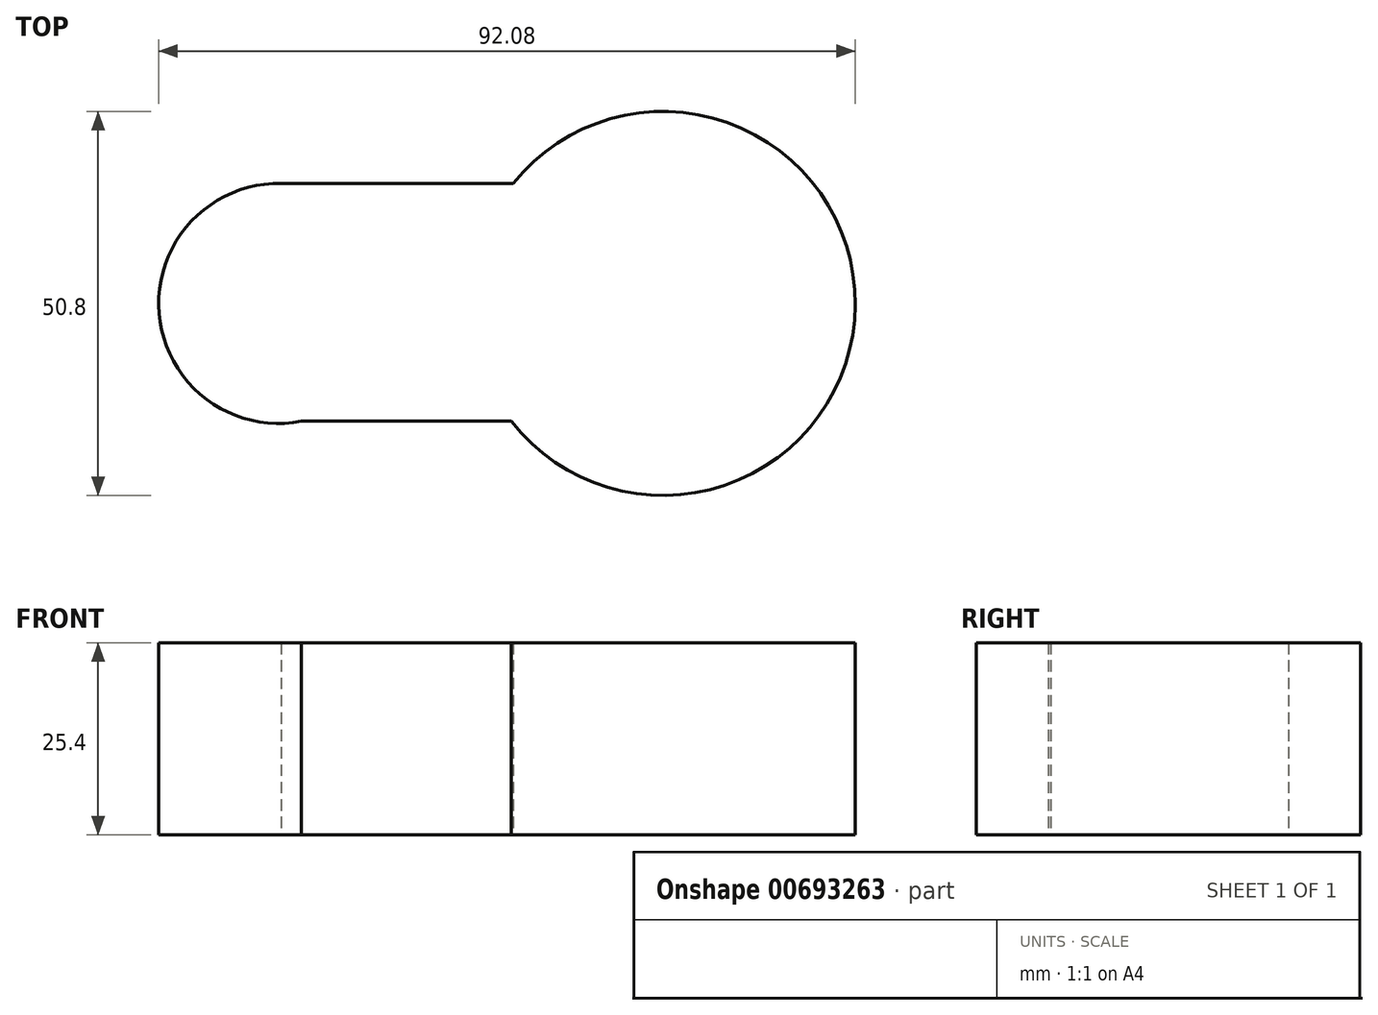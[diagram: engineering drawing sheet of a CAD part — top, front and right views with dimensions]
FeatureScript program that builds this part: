
annotation { "Feature Type Name" : "Feature", "Feature Type Description" : "" }
export const myFeature = defineFeature(function(context is Context, id is Id, definition is map)
    precondition{}
    {
        {
            var Q0;
            Q0=qCreatedBy(makeId("Top.planeOp"),FACE);
            var sketch = newSketch(context, id + "F0", { "sketchPlane" : qUnion([Q0])});
            skCircle(sketch, "E0", {"center": v(-29.75, 0) * mm, "radius": 15.88 * mm});
            skCircle(sketch, "E1", {"center": v(21.05, 0) * mm, "radius": 25.4 * mm});
            skLineSegment(sketch, "E2", {"start": v(-30.1, 15.87) * mm, "end": v(1.22, 15.87) * mm});
            skLineSegment(sketch, "E3", {"start": v(-32.76, -15.59) * mm, "end": v(1, -15.59) * mm});
            skSolve(sketch);
        }
        {
            var Q0;
            {var subQ0=sQuery(id+"F0.wireOp",EDGE,"E2");var subQ1=sQuery(id+"F0.wireOp",EDGE,"E0");var subQ2=makeQuery(id+"F0.imprint","INTERSECT",VERTEX,{"disambiguationData":[OD(0.0)],"derivedFrom":[subQ1,subQ0]});Q0=makeQuery(id+"F0.imprint","IMPRINT",FACE,{"disambiguationData":[TD([[makeQuery(id+"F0.imprint","IMPRINT",EDGE,{"disambiguationData":[TD([[subQ2,-1.0]])],"derivedFrom":subQ1}),1.0]])]});}
            var Q1;
            {var subQ0=sQuery(id+"F0.wireOp",EDGE,"E2");var subQ1=sQuery(id+"F0.wireOp",EDGE,"E0");var subQ2=makeQuery(id+"F0.imprint","INTERSECT",VERTEX,{"disambiguationData":[OD(1.0)],"derivedFrom":[subQ1,subQ0]});Q1=makeQuery(id+"F0.imprint","IMPRINT",FACE,{"disambiguationData":[TD([[makeQuery(id+"F0.imprint","IMPRINT",EDGE,{"disambiguationData":[TD([[subQ2,1.0]])],"derivedFrom":subQ1}),-1.0]])]});}
            extrude(context, id + "F1", {"entities" : qUnion([Q0, Q1]), "depth" : 12.7 * mm, "offsetDistance" : 25.4 * mm});
        }
        {
            var Q0;
            Q0 = qSketchRegion(id + "F0", true);
            var Q1;
            Q1=makeQuery(id+"F1.opExtrude","SWEPT_FACE",FACE,{"disambiguationData":[OSD([sQuery(id+"F0.wireOp",EDGE,"E3")])]});
            extrude(context, id + "F2", {"entities" : qUnion([Q0, Q1]), "operationType" : NewBodyOperationType.ADD, "depth" : 25.4 * mm, "offsetDistance" : 25.4 * mm});
        }
    });
